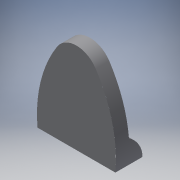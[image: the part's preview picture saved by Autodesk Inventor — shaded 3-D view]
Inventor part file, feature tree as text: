
AUTODESK INVENTOR PART (.ipt)
format: ipt  version: 2016 (Build 200138000, 138)  size: 167,936 bytes
history: native  units: in
note: dims shown in document units (in); Inventor stores cm internally (conversion verified against a paired STEP export)
features: sketch x5, extrude x4, projected_geometry x3, reference x1
ambient origin geometry x8: Origin, YZ Plane, XZ Plane, XY Plane, X Axis, Y Axis, Z Axis, Center Point
bodies: Solid1 (feature_tree)
feature tree (13):
  extrude  "Extrusion1"  Depth=1.0in
  extrude  "Extrusion2"  Depth=0.3937in TaperAngle=0.0deg
  extrude  "Extrusion3"  Depth=1.0in
  extrude  "Extrusion4"  Depth=1.0in TaperAngle=0.0deg
  sketch  "Sketch5"  dims[d12=1.0in d13=0.0in d14=0.5in]
  sketch  "Sketch1"  dims[d0=4.5in d1=1.0in]
  reference  "Reference1"
  sketch  "Sketch2"  dims[d2=0.1969in d3=0.0in d4=0.3937in d5=0.0in]
  projected_geometry  "Projected Loop1"
  sketch  "Sketch3"  dims[d6=0.9843in d7=1.0in]
  sketch  "Sketch4"  dims[d8=4.0in d9=0.0in d10=1.0in d11=0.0in]
  projected_geometry  "Projected Loop2"
  projected_geometry  "Projected Loop3"
